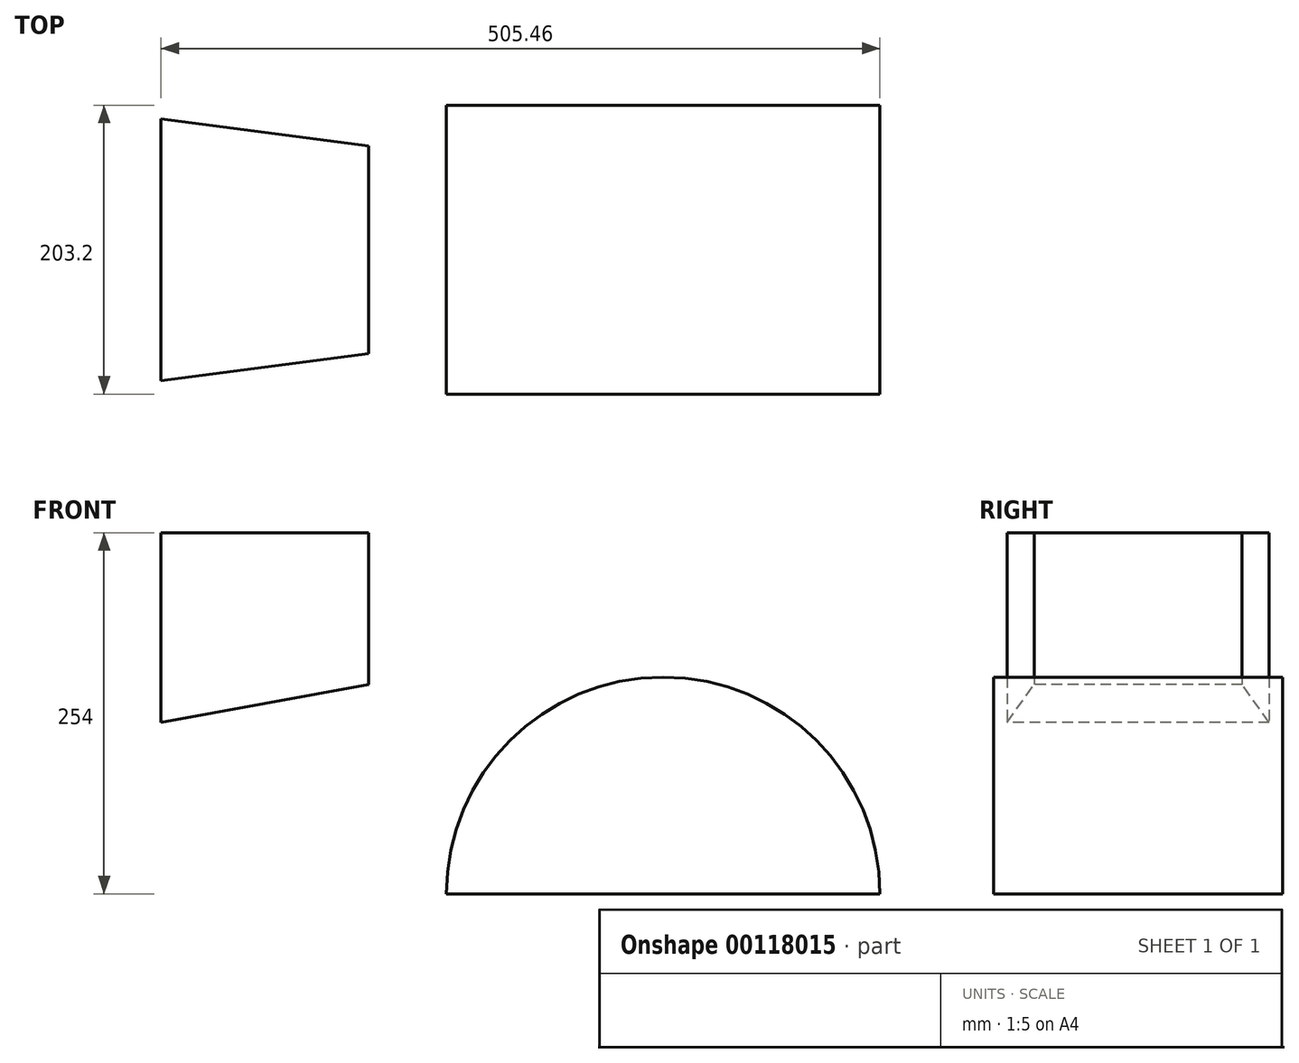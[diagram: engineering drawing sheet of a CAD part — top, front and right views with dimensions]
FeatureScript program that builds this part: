
annotation { "Feature Type Name" : "Feature", "Feature Type Description" : "" }
export const myFeature = defineFeature(function(context is Context, id is Id, definition is map)
    precondition{}
    {
        {
            var Q0;
            Q0=qCreatedBy(makeId("Front.planeOp"),FACE);
            var sketch = newSketch(context, id + "F0", { "sketchPlane" : qUnion([Q0])});
            skArc(sketch, "E0", {"start": v(152.4, 0) * mm, "mid": v(0, 152.4) * mm, "end": v(-152.4, 0) * mm});
            skLineSegment(sketch, "E1", {"start": v(-152.4, 0) * mm, "end": v(152.4, 0) * mm});
            skSolve(sketch);
        }
        {
            var Q0;
            Q0=makeQuery(id+"F0.imprint","IMPRINT",FACE,{"disambiguationData":[TD([[makeQuery(id+"F0.imprint","IMPRINT",EDGE,{"derivedFrom":sQuery(id+"F0.wireOp",EDGE,"E0")}),1.0]])]});
            extrude(context, id + "F1", {"entities" : qUnion([Q0]), "endBound" : BoundingType.SYMMETRIC, "depth" : 203.2 * mm});
        }
        {
            var Q0;
            Q0=qCreatedBy(makeId("Front.planeOp"),FACE);
            var sketch = newSketch(context, id + "F2", { "sketchPlane" : qUnion([Q0])});
            skLineSegment(sketch, "E2", {"start": v(-353.06, 254) * mm, "end": v(-101.6, 254) * mm});
            skPoint(sketch, "E3", {"position": v(-207.01, 254) * mm});
            skArc(sketch, "E4", {"start": v(152.4, 0) * mm, "mid": v(78, 179.6) * mm, "end": v(-101.6, 254) * mm});
            skPoint(sketch, "E5.orphan", {"position": v(0, 232.8) * mm});
            skSolve(sketch);
        }
        {
            var Q0;
            Q0=sQuery(id+"F2.wireOp",EDGE,"E2");
            var Q1;
            Q1=sQuery(id+"F2.wireOp",VERTEX,"E2.start");
            cPlane(context, id + "F3", {"entities" : qUnion([Q0, Q1]), "cplaneType" : CPlaneType.CURVE_POINT, "offset" : 25.4 * mm, "width" : 152.4 * mm, "height" : 152.4 * mm});
        }
        {
            var Q0;
            Q0=sQuery(id+"F2.wireOp",EDGE,"E2");
            var Q1;
            Q1=sQuery(id+"F2.wireOp",VERTEX,"E3");
            cPlane(context, id + "F4", {"entities" : qUnion([Q0, Q1]), "cplaneType" : CPlaneType.CURVE_POINT, "offset" : 25.4 * mm, "width" : 152.4 * mm, "height" : 152.4 * mm});
        }
        {
            var Q0;
            Q0=qCreatedBy(id+"F4.planeOp",FACE);
            var sketch = newSketch(context, id + "F5", { "sketchPlane" : qUnion([Q0])});
            skLineSegment(sketch, "E6.bottom", {"start": v(73.02, 254) * mm, "end": v(-73.03, 254) * mm});
            skLineSegment(sketch, "E6.top", {"start": v(73.03, 147.32) * mm, "end": v(-73.03, 147.32) * mm});
            skLineSegment(sketch, "E6.left", {"start": v(73.02, 254) * mm, "end": v(73.02, 147.32) * mm});
            skLineSegment(sketch, "E6.right", {"start": v(-73.03, 254) * mm, "end": v(-73.03, 147.32) * mm});
            skSolve(sketch);
        }
        {
            var Q0;
            Q0=qCreatedBy(id+"F3.planeOp",FACE);
            var sketch = newSketch(context, id + "F6", { "sketchPlane" : qUnion([Q0])});
            skLineSegment(sketch, "E7.bottom", {"start": v(92.07, 254) * mm, "end": v(-92.08, 254) * mm});
            skLineSegment(sketch, "E7.top", {"start": v(92.07, 120.65) * mm, "end": v(-92.07, 120.65) * mm});
            skLineSegment(sketch, "E7.left", {"start": v(92.07, 254) * mm, "end": v(92.07, 120.65) * mm});
            skLineSegment(sketch, "E7.right", {"start": v(-92.08, 254) * mm, "end": v(-92.07, 120.65) * mm});
            skSolve(sketch);
        }
        {
            var Q0;
            Q0=makeQuery(id+"F6.imprint","IMPRINT",FACE,{"disambiguationData":[TD([[makeQuery(id+"F6.imprint","IMPRINT",EDGE,{"derivedFrom":sQuery(id+"F6.wireOp",EDGE,"E7.bottom")}),1.0]])]});
            var Q1;
            Q1=makeQuery(id+"F5.imprint","IMPRINT",FACE,{"disambiguationData":[TD([[makeQuery(id+"F5.imprint","IMPRINT",EDGE,{"derivedFrom":sQuery(id+"F5.wireOp",EDGE,"E6.bottom")}),1.0]])]});
            loft(context, id + "F7", {"sheetProfilesArray" : [{ "sheetProfileEntities" : qUnion([Q0]) }, { "sheetProfileEntities" : qUnion([Q1]) }]});
        }
    });
